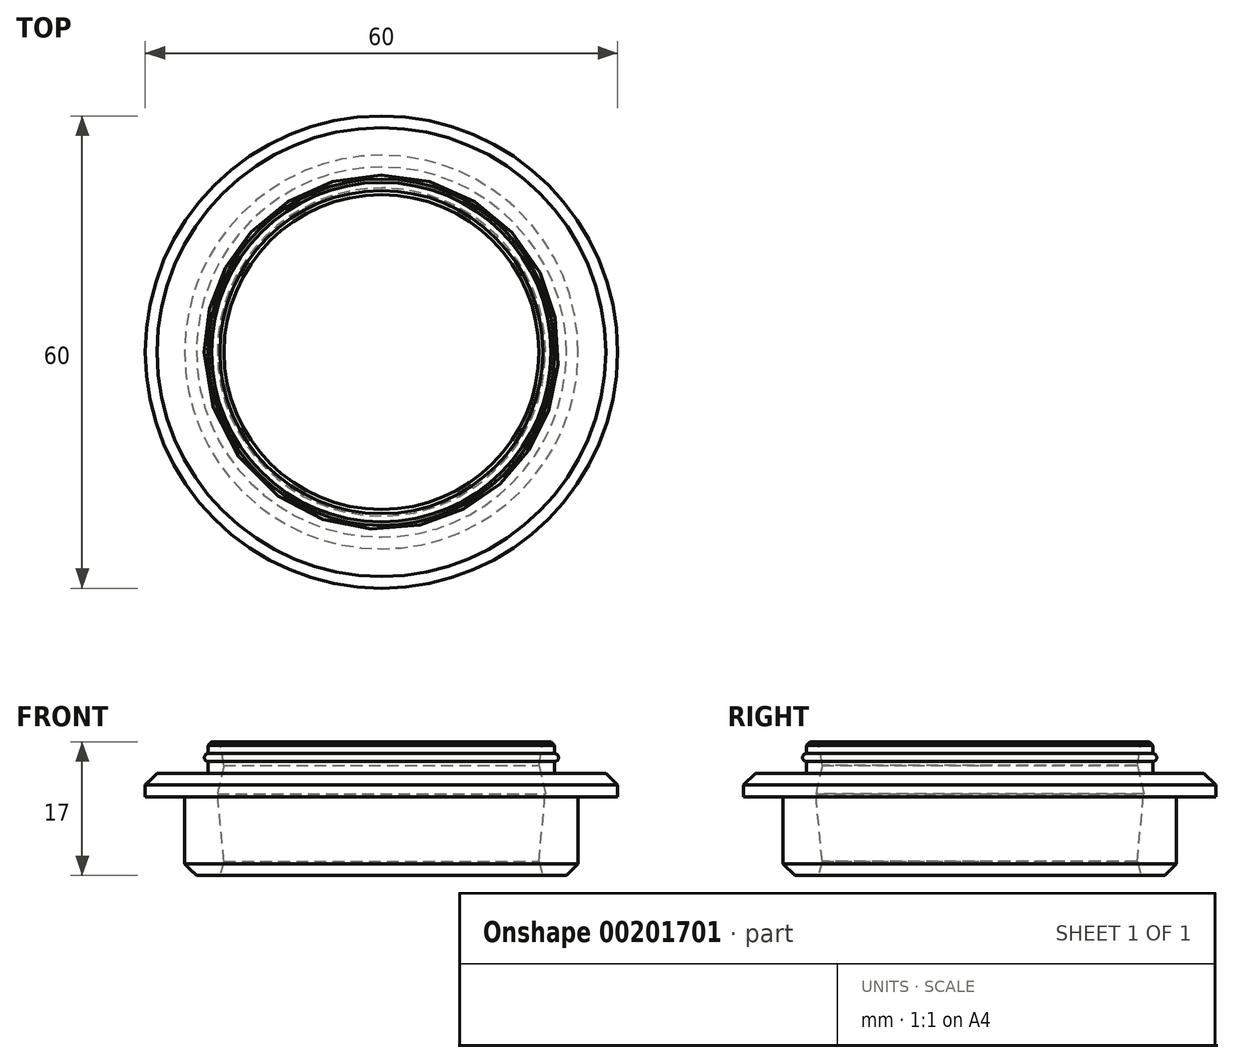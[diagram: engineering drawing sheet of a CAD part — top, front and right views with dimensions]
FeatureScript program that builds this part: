
annotation { "Feature Type Name" : "Feature", "Feature Type Description" : "" }
export const myFeature = defineFeature(function(context is Context, id is Id, definition is map)
    precondition{}
    {
        {
            var Q0;
            Q0=qCreatedBy(makeId("Front.planeOp"),FACE);
            var sketch = newSketch(context, id + "F0", { "sketchPlane" : qUnion([Q0])});
            skLineSegment(sketch, "E0", {"start": v(0, 0) * mm, "end": v(0, 42.45) * mm, "construction": true});
            skLineSegment(sketch, "E1.bottom", {"start": v(-20.54, 0) * mm, "end": v(-23.5, 0) * mm});
            skLineSegment(sketch, "E1.right", {"start": v(-25, 1.5) * mm, "end": v(-25, 10) * mm});
            skLineSegment(sketch, "E2", {"start": v(-25, 10) * mm, "end": v(-30, 10) * mm});
            skLineSegment(sketch, "E3", {"start": v(-30, 10) * mm, "end": v(-30, 11.5) * mm});
            skLineSegment(sketch, "E4", {"start": v(-28.5, 13) * mm, "end": v(-22, 13) * mm});
            skLineSegment(sketch, "E5", {"start": v(-22, 13) * mm, "end": v(-22, 14.5) * mm});
            skLineSegment(sketch, "E6", {"start": v(-21.56, 17) * mm, "end": v(-20.52, 17) * mm});
            skArc(sketch, "E7", {"start": v(-22, 15.5) * mm, "mid": v(-22.5, 15) * mm, "end": v(-22, 14.5) * mm});
            skLineSegment(sketch, "E8.trimOffspring", {"start": v(-22, 15.5) * mm, "end": v(-22, 16.56) * mm});
            skLineSegment(sketch, "E9", {"start": v(-20.54, 0) * mm, "end": v(-20, 1.78) * mm});
            skLineSegment(sketch, "E10", {"start": v(-20, 1.78) * mm, "end": v(-20.83, 10.4) * mm});
            skLineSegment(sketch, "E11", {"start": v(-20.83, 10.4) * mm, "end": v(-20, 14) * mm});
            skLineSegment(sketch, "E12", {"start": v(-20, 14) * mm, "end": v(-20.52, 17) * mm});
            skPoint(sketch, "E13.start.orphan", {"position": v(-20, 17) * mm});
            skPoint(sketch, "E14.orphan", {"position": v(-20, 0) * mm});
            skLineSegment(sketch, "E15", {"start": v(-30, 11.5) * mm, "end": v(-28.5, 13) * mm});
            skPoint(sketch, "E16.orphan", {"position": v(-30, 13) * mm});
            skLineSegment(sketch, "E17", {"start": v(-22, 16.56) * mm, "end": v(-21.56, 17) * mm});
            skPoint(sketch, "E18.orphan", {"position": v(-22, 17) * mm});
            skLineSegment(sketch, "E19", {"start": v(-23.5, 0) * mm, "end": v(-25, 1.5) * mm});
            skSolve(sketch);
        }
        {
            var Q0;
            Q0=qSketchRegion(id+"F0",true);
            var Q1;
            Q1=sQuery(id+"F0.wireOp",EDGE,"E0");
            revolve(context, id + "F1", {"entities" : qUnion([Q0]), "axis" : qUnion([Q1]), "revolveType" : RevolveType.FULL});
        }
    });
